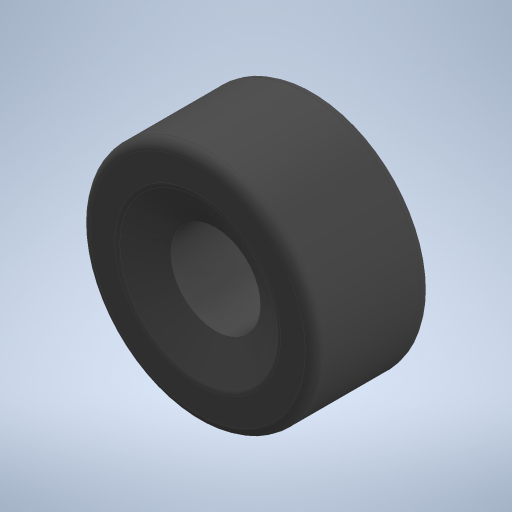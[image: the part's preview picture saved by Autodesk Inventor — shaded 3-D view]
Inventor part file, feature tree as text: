
AUTODESK INVENTOR PART (.ipt)
format: ipt  version: 2023 (Build 270158000, 158)  size: 288,256 bytes
history: native  units: in
note: dims shown in document units (in); Inventor stores cm internally (conversion verified against a paired STEP export)
features: sketch x3, extrude x1, hole x1, revolve x1, plane x1, mirror x1, fillet x1
ambient origin geometry x8: Origin, YZ Plane, XZ Plane, XY Plane, X Axis, Y Axis, Z Axis, Center Point
bodies: Solid1 (feature_tree)
feature tree (9):
  extrude  "Extrusion1"  Depth=0.5118in TaperAngle=0.0deg
  hole  "Hole1"  [1 undecoded]
  revolve  "Revolution1"  Angle=90.0deg
  plane  "Work Plane1"
  mirror  "Mirror1"
  fillet  "Fillet1"  Radius=0.0394in
  sketch  "Sketch1"  dims[d0=1.0236in d1=0.5118in d2=0.0in]
  sketch  "Sketch2"  dims[d3=0.3937in d4=0.2362in d5=0.1575in d6=0.0787in d7=90.0deg d8=0.315in d9=0.8108in d10=0.0787in]
  sketch  "Sketch3"  dims[d11=0.1575in d12=90.0deg d13=0.0394in d14=0.0in d15=0.0in d16=0.0in]
note: 1 required parameter value undecoded (feature->parameter linkage not recoverable at this tier; creation-order binding heuristic only, values carry confidence <= 0.55)
